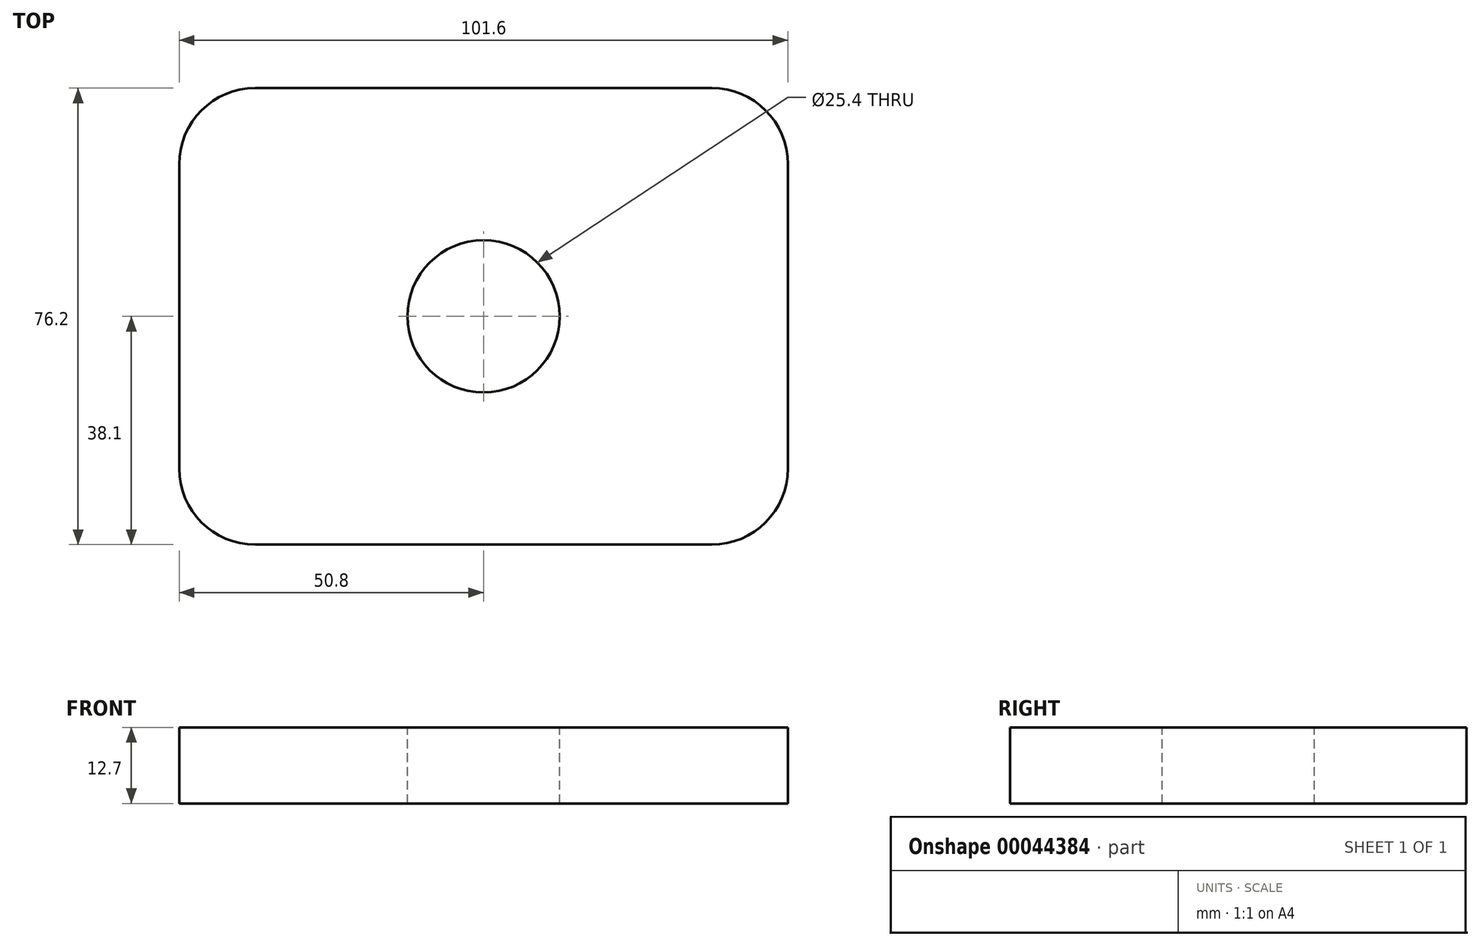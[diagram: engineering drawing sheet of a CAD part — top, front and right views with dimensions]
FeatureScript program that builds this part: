
annotation { "Feature Type Name" : "Feature", "Feature Type Description" : "" }
export const myFeature = defineFeature(function(context is Context, id is Id, definition is map)
    precondition{}
    {
        {
            assignVariable(context, id + "F0", {"name" : "config", "numberValue" : 0, "variableType" : VariableType.NUMBER});
        }
        {
            assignVariable(context, id + "F1", {"name" : "height", "anyValue" : [12.7 * mm, 19.05 * mm, 25.4 * mm][getVariable(context, 'config')]});
        }
        {
            var Q0;
            Q0=qCreatedBy(makeId("Top.planeOp"),FACE);
            var sketch = newSketch(context, id + "F2", { "sketchPlane" : qUnion([Q0])});
            skLineSegment(sketch, "E0.rect.bottom", {"start": v(-50.8, 38.1) * mm, "end": v(50.8, 38.1) * mm});
            skLineSegment(sketch, "E0.rect.top", {"start": v(-50.8, -38.1) * mm, "end": v(50.8, -38.1) * mm});
            skLineSegment(sketch, "E0.rect.left", {"start": v(-50.8, 38.1) * mm, "end": v(-50.8, -38.1) * mm});
            skLineSegment(sketch, "E0.rect.right", {"start": v(50.8, 38.1) * mm, "end": v(50.8, -38.1) * mm});
            skPoint(sketch, "E0.rect.middle", {"position": v(0, 0) * mm});
            skSolve(sketch);
        }
        {
            var Q0;
            Q0=makeQuery(id+"F2.imprint","IMPRINT",FACE,{"disambiguationData":[TD([[makeQuery(id+"F2.imprint","IMPRINT",EDGE,{"derivedFrom":sQuery(id+"F2.wireOp",EDGE,"E0.rect.bottom")}),-1.0]])]});
            extrude(context, id + "F3", {"entities" : qUnion([Q0]), "depth" : getVariable(context, 'height')});
        }
        {
            var Q0;
            Q0=makeQuery(id+"F3.opExtrude","SWEPT_EDGE",EDGE,{"disambiguationData":[OSD([sQuery(id+"F2.wireOp",EDGE,"E0.rect.top"),sQuery(id+"F2.wireOp",EDGE,"E0.rect.left")])]});
            var Q1;
            Q1=makeQuery(id+"F3.opExtrude","SWEPT_EDGE",EDGE,{"disambiguationData":[OSD([sQuery(id+"F2.wireOp",EDGE,"E0.rect.top"),sQuery(id+"F2.wireOp",EDGE,"E0.rect.right")])]});
            var Q2;
            Q2=makeQuery(id+"F3.opExtrude","SWEPT_EDGE",EDGE,{"disambiguationData":[OSD([sQuery(id+"F2.wireOp",EDGE,"E0.rect.bottom"),sQuery(id+"F2.wireOp",EDGE,"E0.rect.right")])]});
            var Q3;
            Q3=makeQuery(id+"F3.opExtrude","SWEPT_EDGE",EDGE,{"disambiguationData":[OSD([sQuery(id+"F2.wireOp",EDGE,"E0.rect.bottom"),sQuery(id+"F2.wireOp",EDGE,"E0.rect.left")])]});
            fillet(context, id + "F4", {"entities" : qUnion([Q0, Q1, Q2, Q3]), "radius" : [12.7 * mm, 19.05 * mm, 1 * degree][getVariable(context, 'config')], "tangentPropagation" : true, "allowEdgeOverflow" : false});
        }
        {
            var Q0;
            Q0=makeQuery(id+"F3.opExtrude","CAP_FACE",FACE,{"disambiguationData":[OSD([sQuery(id+"F2.wireOp",EDGE,"E0.rect.bottom"),sQuery(id+"F2.wireOp",EDGE,"E0.rect.top"),sQuery(id+"F2.wireOp",EDGE,"E0.rect.left"),sQuery(id+"F2.wireOp",EDGE,"E0.rect.right")])],"isStart":false});
            var sketch = newSketch(context, id + "F5", { "sketchPlane" : qUnion([Q0])});
            skCircle(sketch, "E1", {"center": v(0, 0) * mm, "radius": 12.7 * mm});
            skSolve(sketch);
        }
        {
            var Q0;
            Q0=makeQuery(id+"F5.imprint","IMPRINT",FACE,{"disambiguationData":[TD([[makeQuery(id+"F5.imprint","IMPRINT",EDGE,{"derivedFrom":sQuery(id+"F5.wireOp",EDGE,"E1")}),1.0]])]});
            extrude(context, id + "F6", {"entities" : qUnion([Q0]), "operationType" : NewBodyOperationType.REMOVE, "oppositeDirection" : true, "depth" : [getVariable(context, 'height'), 1 * degree, getVariable(context, 'height')][getVariable(context, 'config')]});
        }
    });
